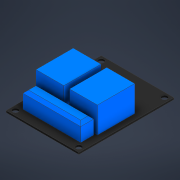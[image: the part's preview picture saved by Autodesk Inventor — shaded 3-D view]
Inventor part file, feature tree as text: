
AUTODESK INVENTOR PART (.ipt)
format: ipt  version: 2021 (Build 250183000, 183)  size: 145,408 bytes
history: native  units: mm
features: extrude x3, other x1, sketch x1, chamfer x1
ambient origin geometry x8: Origin, YZ Plane, XZ Plane, XY Plane, X Axis, Y Axis, Z Axis, Center Point
bodies: Volumenkörper1 (feature_tree)
feature tree (6):
  other  "Relais"
  sketch  "Skizze1"  dims[d0=39.0mm d1=51.0mm d2=3.0mm d3=2.5mm d4=2.5mm d5=7.0mm d6=5.0mm d7=31.0mm d8=15.0mm d9=20.0mm d10=1.0mm d11=0.0mm d12=10.0mm d13=0.0mm d14=15.0mm d15=0.0mm d16=1.5mm d17=2.0mm d18=45.0deg d19=3.0mm d20=13.0mm]
  extrude  "Extrusion1"  Depth=51.0mm
  extrude  "Extrusion2"  Depth=3.0mm
  extrude  "Extrusion3"  Depth=13.0mm
  chamfer  "Fase1"  Distance=2.5mm
